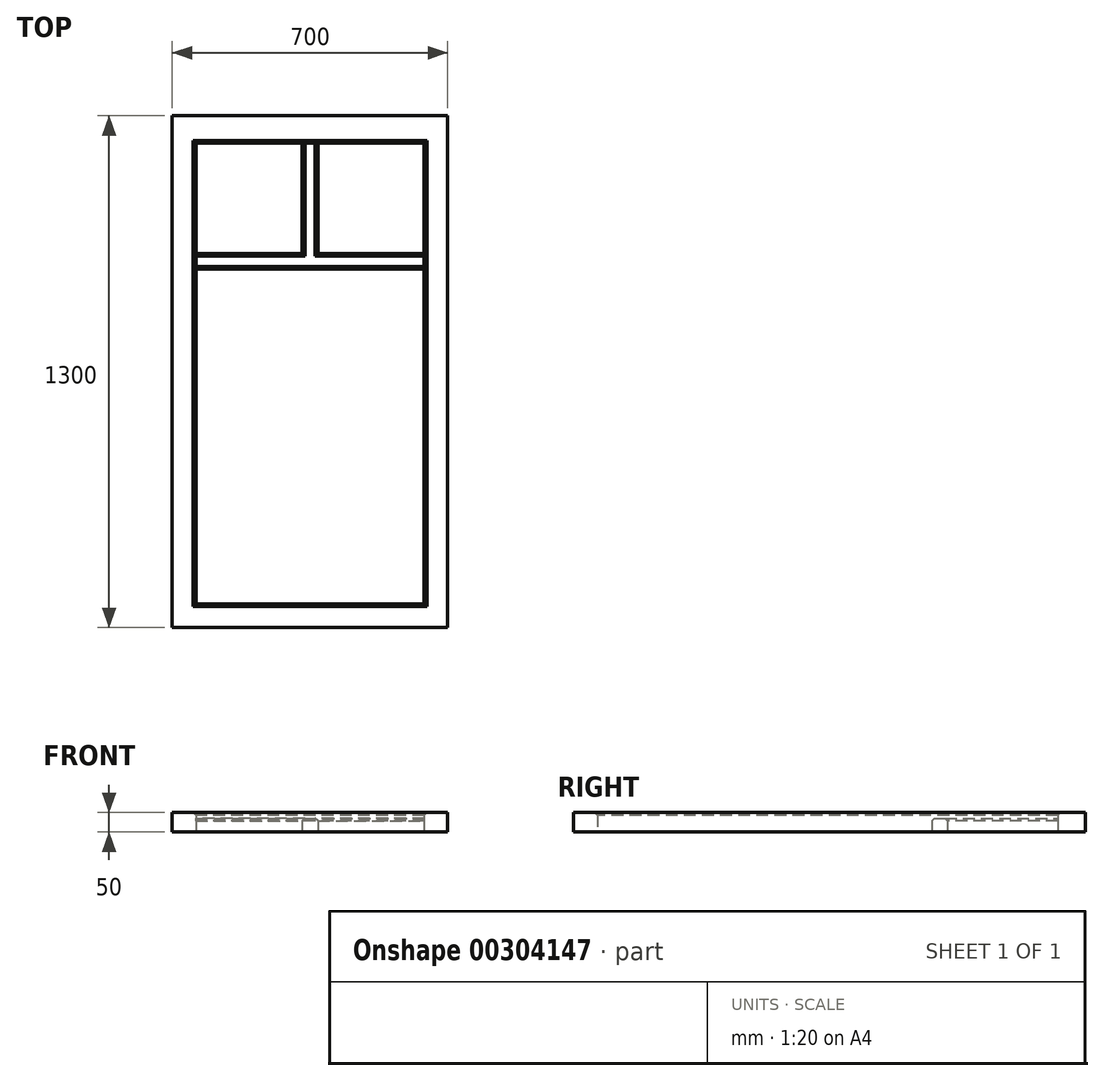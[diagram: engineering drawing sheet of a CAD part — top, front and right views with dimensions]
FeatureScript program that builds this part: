
annotation { "Feature Type Name" : "Feature", "Feature Type Description" : "" }
export const myFeature = defineFeature(function(context is Context, id is Id, definition is map)
    precondition{}
    {
        {
            var Q0;
            Q0=qCreatedBy(makeId("Top.planeOp"),FACE);
            var sketch = newSketch(context, id + "F0", { "sketchPlane" : qUnion([Q0])});
            skLineSegment(sketch, "E0.bottom", {"start": v(-321.69, 765.2) * mm, "end": v(378.31, 765.2) * mm});
            skLineSegment(sketch, "E0.top", {"start": v(-321.69, -534.8) * mm, "end": v(378.31, -534.8) * mm});
            skLineSegment(sketch, "E0.left", {"start": v(-321.69, 765.2) * mm, "end": v(-321.69, -534.8) * mm});
            skLineSegment(sketch, "E0.right", {"start": v(378.31, 765.2) * mm, "end": v(378.31, -534.8) * mm});
            skLineSegment(sketch, "E1.bottom", {"start": v(-261.69, 695.2) * mm, "end": v(8.31, 695.2) * mm});
            skLineSegment(sketch, "E1.top", {"start": v(-261.69, 415.2) * mm, "end": v(8.31, 415.2) * mm});
            skLineSegment(sketch, "E1.left", {"start": v(-261.69, 695.2) * mm, "end": v(-261.69, 415.2) * mm});
            skLineSegment(sketch, "E1.right", {"start": v(8.31, 695.2) * mm, "end": v(8.31, 415.2) * mm});
            skLineSegment(sketch, "E2.bottom", {"start": v(48.31, 695.2) * mm, "end": v(318.31, 695.2) * mm});
            skLineSegment(sketch, "E2.top", {"start": v(48.31, 415.2) * mm, "end": v(318.31, 415.2) * mm});
            skLineSegment(sketch, "E2.left", {"start": v(48.31, 695.2) * mm, "end": v(48.31, 415.2) * mm});
            skLineSegment(sketch, "E2.right", {"start": v(318.31, 695.2) * mm, "end": v(318.31, 415.2) * mm});
            skLineSegment(sketch, "E3.bottom", {"start": v(-261.69, 375.2) * mm, "end": v(318.31, 375.2) * mm});
            skLineSegment(sketch, "E3.top", {"start": v(-261.69, -474.8) * mm, "end": v(318.31, -474.8) * mm});
            skLineSegment(sketch, "E3.left", {"start": v(-261.69, 375.2) * mm, "end": v(-261.69, -474.8) * mm});
            skLineSegment(sketch, "E3.right", {"start": v(318.31, 375.2) * mm, "end": v(318.31, -474.8) * mm});
            skLineSegment(sketch, "E4", {"start": v(-261.69, 375.2) * mm, "end": v(-261.69, 415.2) * mm});
            skLineSegment(sketch, "E5", {"start": v(8.31, 695.2) * mm, "end": v(48.31, 695.2) * mm});
            skLineSegment(sketch, "E6", {"start": v(318.31, 415.2) * mm, "end": v(318.31, 375.2) * mm});
            skSolve(sketch);
        }
        {
            var Q0;
            Q0=makeQuery(id+"F0.imprint","IMPRINT",FACE,{"disambiguationData":[TD([[makeQuery(id+"F0.imprint","IMPRINT",EDGE,{"derivedFrom":sQuery(id+"F0.wireOp",EDGE,"E0.bottom")}),-1.0]])]});
            extrude(context, id + "F1", {"entities" : qUnion([Q0]), "depth" : 50 * mm, "offsetDistance" : 25 * mm});
        }
        {
            var Q0;
            Q0=makeQuery(id+"F0.imprint","IMPRINT",FACE,{"disambiguationData":[TD([[makeQuery(id+"F0.imprint","IMPRINT",EDGE,{"derivedFrom":sQuery(id+"F0.wireOp",EDGE,"E1.top")}),-1.0]])]});
            extrude(context, id + "F2", {"entities" : qUnion([Q0]), "depth" : 35 * mm, "offsetDistance" : 25 * mm});
        }
        {
            var Q0;
            Q0=makeQuery(id+"F1.opExtrude","CAP_EDGE",EDGE,{"disambiguationData":[OSD([sQuery(id+"F0.wireOp",EDGE,"E3.bottom")])],"isStart":false});
            var Q1;
            Q1=makeQuery(id+"F1.opExtrude","CAP_EDGE",EDGE,{"disambiguationData":[OSD([sQuery(id+"F0.wireOp",EDGE,"E3.right")])],"isStart":false});
            var Q2;
            Q2=makeQuery(id+"F1.opExtrude","CAP_EDGE",EDGE,{"disambiguationData":[OSD([sQuery(id+"F0.wireOp",EDGE,"mo2UJA6X-26PH-taNp-pn0z-x9dp37UM4p0T.bottom")])],"isStart":false});
            var Q3;
            Q3=makeQuery(id+"F1.opExtrude","CAP_EDGE",EDGE,{"disambiguationData":[OSD([sQuery(id+"F0.wireOp",EDGE,"Al6UGsGZ-SmRB-BLA8-lGx7-s1gn5zOmxmS4.right")])],"isStart":false});
            var Q4;
            Q4=makeQuery(id+"F1.opExtrude","CAP_EDGE",EDGE,{"disambiguationData":[OSD([sQuery(id+"F0.wireOp",EDGE,"Al6UGsGZ-SmRB-BLA8-lGx7-s1gn5zOmxmS4.left")])],"isStart":false});
            var Q5;
            Q5=makeQuery(id+"F1.opExtrude","CAP_EDGE",EDGE,{"disambiguationData":[OSD([sQuery(id+"F0.wireOp",EDGE,"Al6UGsGZ-SmRB-BLA8-lGx7-s1gn5zOmxmS4.top")])],"isStart":false});
            var Q6;
            Q6=makeQuery(id+"F1.opExtrude","CAP_EDGE",EDGE,{"disambiguationData":[OSD([sQuery(id+"F0.wireOp",EDGE,"E1.top")])],"isStart":false});
            var Q7;
            Q7=makeQuery(id+"F1.opExtrude","CAP_EDGE",EDGE,{"disambiguationData":[OSD([sQuery(id+"F0.wireOp",EDGE,"E1.right")])],"isStart":false});
            var Q8;
            Q8=makeQuery(id+"F1.opExtrude","CAP_EDGE",EDGE,{"disambiguationData":[OSD([sQuery(id+"F0.wireOp",EDGE,"E1.bottom")])],"isStart":false});
            var Q9;
            Q9=makeQuery(id+"F1.opExtrude","CAP_EDGE",EDGE,{"disambiguationData":[OSD([sQuery(id+"F0.wireOp",EDGE,"E1.left")])],"isStart":false});
            var Q10;
            Q10=makeQuery(id+"F1.opExtrude","CAP_EDGE",EDGE,{"disambiguationData":[OSD([sQuery(id+"F0.wireOp",EDGE,"Al6UGsGZ-SmRB-BLA8-lGx7-s1gn5zOmxmS4.bottom")])],"isStart":false});
            var Q11;
            Q11=makeQuery(id+"F1.opExtrude","CAP_EDGE",EDGE,{"disambiguationData":[OSD([sQuery(id+"F0.wireOp",EDGE,"E2.bottom")])],"isStart":false});
            var Q12;
            Q12=makeQuery(id+"F1.opExtrude","CAP_EDGE",EDGE,{"disambiguationData":[OSD([sQuery(id+"F0.wireOp",EDGE,"E2.left")])],"isStart":false});
            var Q13;
            Q13=makeQuery(id+"F1.opExtrude","CAP_EDGE",EDGE,{"disambiguationData":[OSD([sQuery(id+"F0.wireOp",EDGE,"E2.right")])],"isStart":false});
            var Q14;
            Q14=makeQuery(id+"F1.opExtrude","CAP_EDGE",EDGE,{"disambiguationData":[OSD([sQuery(id+"F0.wireOp",EDGE,"E2.top")])],"isStart":false});
            var Q15;
            Q15=makeQuery(id+"F1.opExtrude","CAP_EDGE",EDGE,{"disambiguationData":[OSD([sQuery(id+"F0.wireOp",EDGE,"mo2UJA6X-26PH-taNp-pn0z-x9dp37UM4p0T.right")])],"isStart":false});
            var Q16;
            Q16=makeQuery(id+"F1.opExtrude","CAP_EDGE",EDGE,{"disambiguationData":[OSD([sQuery(id+"F0.wireOp",EDGE,"mo2UJA6X-26PH-taNp-pn0z-x9dp37UM4p0T.top")])],"isStart":false});
            var Q17;
            Q17=makeQuery(id+"F1.opExtrude","CAP_EDGE",EDGE,{"disambiguationData":[OSD([sQuery(id+"F0.wireOp",EDGE,"mo2UJA6X-26PH-taNp-pn0z-x9dp37UM4p0T.left")])],"isStart":false});
            var Q18;
            Q18=makeQuery(id+"F1.opExtrude","CAP_EDGE",EDGE,{"disambiguationData":[OSD([sQuery(id+"F0.wireOp",EDGE,"E3.top")])],"isStart":false});
            var Q19;
            Q19=makeQuery(id+"F1.opExtrude","CAP_EDGE",EDGE,{"disambiguationData":[OSD([sQuery(id+"F0.wireOp",EDGE,"E3.left")])],"isStart":false});
            var Q20;
            Q20=makeQuery(id+"F2.opExtrude","CAP_EDGE",EDGE,{"disambiguationData":[OSD([sQuery(id+"F0.wireOp",EDGE,"E1.right")])],"isStart":false});
            var Q21;
            Q21=makeQuery(id+"F2.opExtrude","CAP_EDGE",EDGE,{"disambiguationData":[OSD([sQuery(id+"F0.wireOp",EDGE,"E2.left")])],"isStart":false});
            var Q22;
            Q22=makeQuery(id+"F2.opExtrude","CAP_EDGE",EDGE,{"disambiguationData":[OSD([sQuery(id+"F0.wireOp",EDGE,"E1.top")])],"isStart":false});
            var Q23;
            Q23=makeQuery(id+"F2.opExtrude","CAP_EDGE",EDGE,{"disambiguationData":[OSD([sQuery(id+"F0.wireOp",EDGE,"E2.top")])],"isStart":false});
            var Q24;
            Q24=makeQuery(id+"F2.opExtrude","CAP_EDGE",EDGE,{"disambiguationData":[OSD([sQuery(id+"F0.wireOp",EDGE,"E3.bottom")])],"isStart":false});
            chamfer(context, id + "F3", {"entities" : qUnion([Q0, Q1, Q2, Q3, Q4, Q5, Q6, Q7, Q8, Q9, Q10, Q11, Q12, Q13, Q14, Q15, Q16, Q17, Q18, Q19, Q20, Q21, Q22, Q23, Q24]), "width" : 7 * mm, "tangentPropagation" : true});
        }
    });
